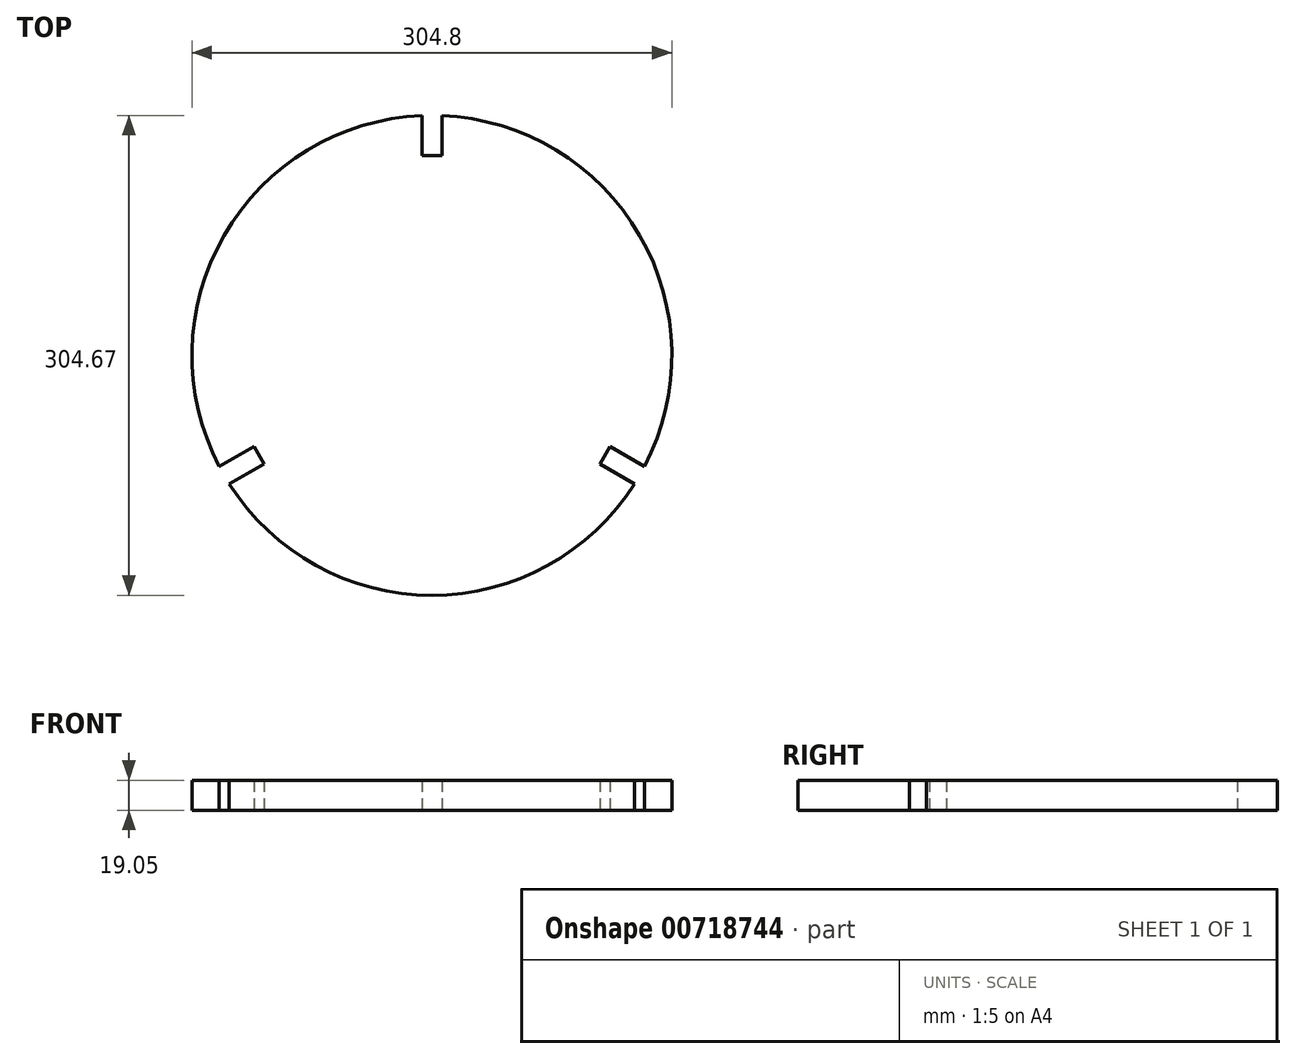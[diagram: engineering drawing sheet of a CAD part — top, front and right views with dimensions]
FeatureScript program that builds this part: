
annotation { "Feature Type Name" : "Feature", "Feature Type Description" : "" }
export const myFeature = defineFeature(function(context is Context, id is Id, definition is map)
    precondition{}
    {
        {
            var Q0;
            Q0=qCreatedBy(makeId("Top.planeOp"),FACE);
            var sketch = newSketch(context, id + "F0", { "sketchPlane" : qUnion([Q0])});
            skCircle(sketch, "E0", {"center": v(0, 0) * mm, "radius": 152.4 * mm});
            skLineSegment(sketch, "E1", {"start": v(0, 0) * mm, "end": v(0, 152.4) * mm, "construction": true});
            skLineSegment(sketch, "E2", {"start": v(0, 0) * mm, "end": v(131.98, -76.2) * mm, "construction": true});
            skLineSegment(sketch, "E3", {"start": v(0, 0) * mm, "end": v(-131.98, -76.2) * mm, "construction": true});
            skLineSegment(sketch, "E4", {"start": v(-6.35, 152.27) * mm, "end": v(-6.35, 126.87) * mm});
            skLineSegment(sketch, "E5", {"start": v(-6.35, 126.87) * mm, "end": v(6.35, 126.87) * mm});
            skLineSegment(sketch, "E6", {"start": v(6.35, 126.87) * mm, "end": v(6.35, 152.27) * mm});
            skLineSegment(sketch, "E7.1.0", {"start": v(-128.7, -81.63) * mm, "end": v(-106.7, -68.93) * mm});
            skLineSegment(sketch, "E7.1.1", {"start": v(-106.7, -68.93) * mm, "end": v(-113.05, -57.93) * mm});
            skLineSegment(sketch, "E7.1.2", {"start": v(-113.05, -57.93) * mm, "end": v(-135.04, -70.63) * mm});
            skLineSegment(sketch, "E7.2.0", {"start": v(135.04, -70.63) * mm, "end": v(113.05, -57.93) * mm});
            skLineSegment(sketch, "E7.2.1", {"start": v(113.05, -57.93) * mm, "end": v(106.7, -68.93) * mm});
            skLineSegment(sketch, "E7.2.2", {"start": v(106.7, -68.93) * mm, "end": v(128.7, -81.63) * mm});
            skSolve(sketch);
        }
        {
            var Q0;
            {var subQ0=sQuery(id+"F0.wireOp",EDGE,"E4");Q0=makeQuery(id+"F0.imprint","IMPRINT",FACE,{"disambiguationData":[TD([[makeQuery(id+"F0.imprint","IMPRINT",EDGE,{"derivedFrom":subQ0}),-1.0]])]});}
            extrude(context, id + "F1", {"entities" : qUnion([Q0]), "depth" : 19.05 * mm, "offsetDistance" : 25.4 * mm});
        }
    });
